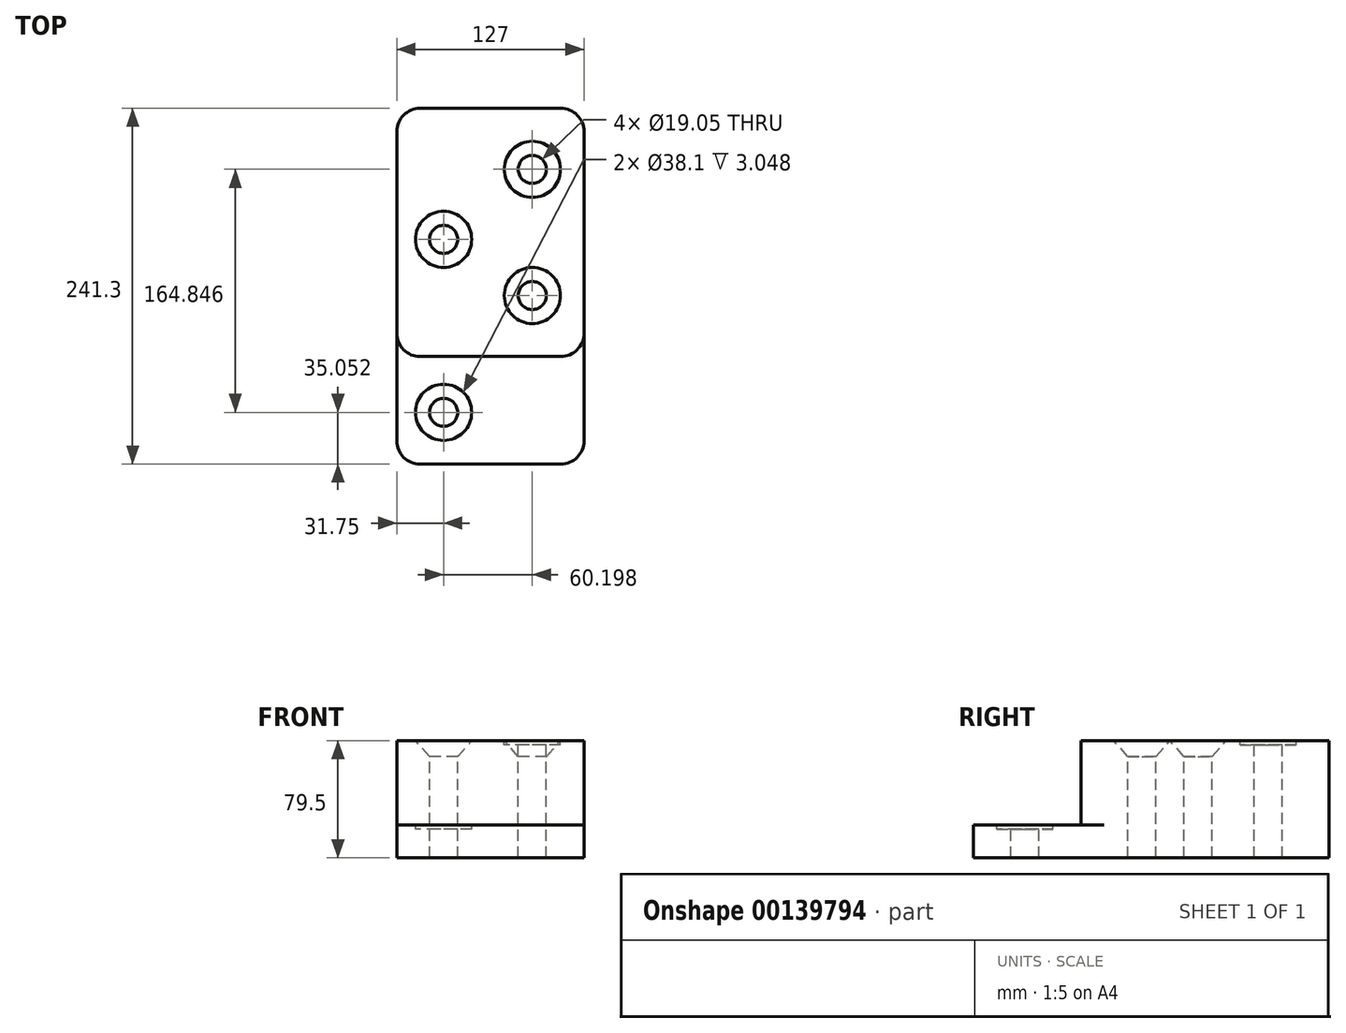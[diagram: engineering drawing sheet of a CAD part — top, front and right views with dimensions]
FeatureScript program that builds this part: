
annotation { "Feature Type Name" : "Feature", "Feature Type Description" : "" }
export const myFeature = defineFeature(function(context is Context, id is Id, definition is map)
    precondition{}
    {
        {
            var Q0;
            Q0=qCreatedBy(makeId("Top.planeOp"),FACE);
            var sketch = newSketch(context, id + "F0", { "sketchPlane" : qUnion([Q0])});
            skLineSegment(sketch, "E0.bottom", {"start": v(-63.5, -120.65) * mm, "end": v(63.5, -120.65) * mm});
            skLineSegment(sketch, "E0.top", {"start": v(-63.5, 120.65) * mm, "end": v(63.5, 120.65) * mm});
            skLineSegment(sketch, "E0.left", {"start": v(-63.5, -120.65) * mm, "end": v(-63.5, 120.65) * mm});
            skLineSegment(sketch, "E0.right", {"start": v(63.5, -120.65) * mm, "end": v(63.5, 120.65) * mm});
            skPoint(sketch, "E0.middle", {"position": v(0, 0) * mm});
            skLineSegment(sketch, "E1", {"start": v(-63.5, -47.75) * mm, "end": v(63.5, -47.75) * mm});
            skPoint(sketch, "E2", {"position": v(28.45, 79.25) * mm});
            skPoint(sketch, "E3", {"position": v(-31.75, 31.75) * mm});
            skPoint(sketch, "E4", {"position": v(28.45, -6.35) * mm});
            skPoint(sketch, "E5", {"position": v(-31.75, -85.6) * mm});
            skSolve(sketch);
        }
        {
            var Q0;
            {var subQ0=sQuery(id+"F0.wireOp",EDGE,"E0.top");Q0=makeQuery(id+"F0.imprint","IMPRINT",FACE,{"disambiguationData":[TD([[makeQuery(id+"F0.imprint","IMPRINT",EDGE,{"derivedFrom":subQ0}),-1.0]])]});}
            extrude(context, id + "F1", {"entities" : qUnion([Q0]), "depth" : 79.5 * mm});
        }
        {
            var Q0;
            {var subQ0=sQuery(id+"F0.wireOp",EDGE,"E0.bottom");Q0=makeQuery(id+"F0.imprint","IMPRINT",FACE,{"disambiguationData":[TD([[makeQuery(id+"F0.imprint","IMPRINT",EDGE,{"derivedFrom":subQ0}),1.0]])]});}
            extrude(context, id + "F2", {"entities" : qUnion([Q0]), "operationType" : NewBodyOperationType.ADD, "depth" : 22.35 * mm});
        }
        {
            var Q0;
            Q0=makeQuery(id+"F1.opExtrude","CAP_FACE",FACE,{"disambiguationData":[OSD([sQuery(id+"F0.wireOp",EDGE,"E0.top"),sQuery(id+"F0.wireOp",EDGE,"E0.left"),sQuery(id+"F0.wireOp",EDGE,"E0.right"),sQuery(id+"F0.wireOp",EDGE,"E1")])],"isStart":false});
            var sketch = newSketch(context, id + "F3", { "sketchPlane" : qUnion([Q0])});
            skPoint(sketch, "E6.0", {"position": v(28.45, 79.25) * mm});
            skPoint(sketch, "E6.1", {"position": v(-31.75, 31.75) * mm});
            skPoint(sketch, "E6.2", {"position": v(28.45, -6.35) * mm});
            skSolve(sketch);
        }
        {
            var Q0;
            Q0=sQuery(id+"F3.wireOp",VERTEX,"E6.1");
            var Q1;
            Q1=sQuery(id+"F3.wireOp",VERTEX,"E6.2");
            var Q2;
            Q2=makeQuery(id+"F1.opExtrude","SWEPT_BODY",BODY,{"disambiguationData":[OSD([sQuery(id+"F0.wireOp",EDGE,"E0.top"),sQuery(id+"F0.wireOp",EDGE,"E0.left"),sQuery(id+"F0.wireOp",EDGE,"E0.right"),sQuery(id+"F0.wireOp",EDGE,"E1")])]});
            hole(context, id + "F4", {"style" : HoleStyle.C_SINK, "endStyle" : HoleEndStyle.THROUGH, "holeDiameter" : 19.05 * mm, "cSinkDiameter" : 38.1 * mm, "cSinkAngle" : 82 * degree, "locations" : qUnion([Q0, Q1]), "scope" : qUnion([Q2]), "isTappedThrough" : true});
        }
        {
            var Q0;
            Q0=makeQuery(id+"F2.opExtrude","CAP_FACE",FACE,{"disambiguationData":[OSD([sQuery(id+"F0.wireOp",EDGE,"E0.bottom"),sQuery(id+"F0.wireOp",EDGE,"E0.left"),sQuery(id+"F0.wireOp",EDGE,"E0.right"),sQuery(id+"F0.wireOp",EDGE,"E1")])],"isStart":false});
            var sketch = newSketch(context, id + "F5", { "sketchPlane" : qUnion([Q0])});
            skPoint(sketch, "E7.0", {"position": v(-31.75, -85.6) * mm});
            skSolve(sketch);
        }
        {
            var Q0;
            Q0=sQuery(id+"F3.wireOp",VERTEX,"E6.0");
            var Q1;
            Q1=sQuery(id+"F5.wireOp",VERTEX,"E7.0");
            var Q2;
            Q2=makeQuery(id+"F1.opExtrude","SWEPT_BODY",BODY,{"disambiguationData":[OSD([sQuery(id+"F0.wireOp",EDGE,"E0.top"),sQuery(id+"F0.wireOp",EDGE,"E0.left"),sQuery(id+"F0.wireOp",EDGE,"E0.right"),sQuery(id+"F0.wireOp",EDGE,"E1")])]});
            hole(context, id + "F6", {"style" : HoleStyle.C_BORE, "endStyle" : HoleEndStyle.THROUGH, "holeDiameter" : 19.05 * mm, "cBoreDiameter" : 38.1 * mm, "cBoreDepth" : 3.05 * mm, "locations" : qUnion([Q0, Q1]), "scope" : qUnion([Q2]), "isTappedThrough" : true});
        }
        {
            var Q0;
            Q0=makeQuery(id+"F1.opExtrude","SWEPT_EDGE",EDGE,{"disambiguationData":[OSD([sQuery(id+"F0.wireOp",EDGE,"E0.left"),sQuery(id+"F0.wireOp",EDGE,"E1")])]});
            var Q1;
            Q1=makeQuery(id+"F1.opExtrude","SWEPT_EDGE",EDGE,{"disambiguationData":[OSD([sQuery(id+"F0.wireOp",EDGE,"E0.right"),sQuery(id+"F0.wireOp",EDGE,"E1")])]});
            var Q2;
            Q2=makeQuery(id+"F2.opExtrude","SWEPT_EDGE",EDGE,{"disambiguationData":[OSD([sQuery(id+"F0.wireOp",EDGE,"E0.bottom"),sQuery(id+"F0.wireOp",EDGE,"E0.right")])]});
            var Q3;
            Q3=makeQuery(id+"F2.opExtrude","SWEPT_EDGE",EDGE,{"disambiguationData":[OSD([sQuery(id+"F0.wireOp",EDGE,"E0.bottom"),sQuery(id+"F0.wireOp",EDGE,"E0.left")])]});
            var Q4;
            Q4=makeQuery(id+"F1.opExtrude","SWEPT_EDGE",EDGE,{"disambiguationData":[OSD([sQuery(id+"F0.wireOp",EDGE,"E0.top"),sQuery(id+"F0.wireOp",EDGE,"E0.left")])]});
            var Q5;
            Q5=makeQuery(id+"F1.opExtrude","SWEPT_EDGE",EDGE,{"disambiguationData":[OSD([sQuery(id+"F0.wireOp",EDGE,"E0.top"),sQuery(id+"F0.wireOp",EDGE,"E0.right")])]});
            fillet(context, id + "F7", {"entities" : qUnion([Q0, Q1, Q2, Q3, Q4, Q5]), "radius" : 15.75 * mm, "tangentPropagation" : true, "allowEdgeOverflow" : false});
        }
    });
